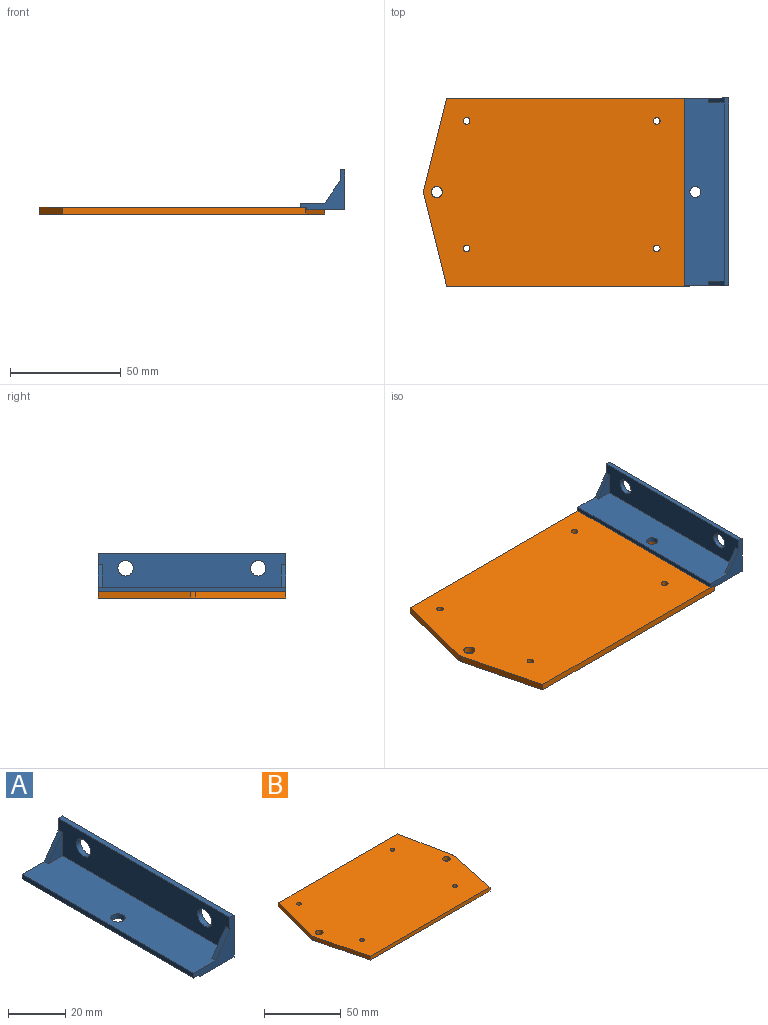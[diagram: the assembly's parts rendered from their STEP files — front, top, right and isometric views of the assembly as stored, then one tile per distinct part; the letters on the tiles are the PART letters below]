
ASSEMBLY  parts=2 mates=1
PART A: 19 faces, bbox 20x85x18 mm
  f0: plane 85x15mm, normal (-1,0,0), area 1158mm2, adj f1,f2,f3,f12,f13,f14,f15,f16
  f1: plane 85x18mm, normal (0,0,1), area 1482.4mm2, adj f0,f2,f3,f4,f5,f15,f16,f17
  f2: plane 20x18mm, normal (0,-1,0), area 122mm2, adj f0,f1,f4,f6,f7,f10,f11,f12
  f3: plane 20x18mm, normal (0,1,0), area 122mm2, adj f0,f1,f4,f6,f8,f10,f11,f12
  f4: plane 85x2mm, normal (-1,0,0), area 170mm2, adj f1,f2,f3,f6
  f5: cylinder r=2.5mm len=5mm, axis (0,0,1), area 31.4mm2, adj f1,f6
  f6: plane 85x11.5mm, normal (0,0,-1), area 602.1mm2, adj f2,f3,f4,f5,f7,f8,f9
  f7: plane 41.21x8.37mm, normal (-0.98,0.2,0), area 42mm2, adj f2,f6,f9,f11
  f8: plane 41.21x8.37mm, normal (-0.98,-0.2,0), area 42mm2, adj f3,f6,f9,f11
  f9: cylinder r=6.5mm len=2.59mm, axis (0,0,1), area 2.6mm2, adj f6,f7,f8,f11
  f10: plane 85x18mm, normal (1,0,0), area 1453mm2, adj f2,f3,f11,f12,f13,f14
  f11: plane 85x17mm, normal (0,0,-1), area 1078.2mm2, adj f2,f3,f7,f8,f9,f10
  f12: plane 85x2mm, normal (0,0,1), area 170mm2, adj f0,f2,f3,f10
  f13: cylinder r=3.5mm len=7mm, axis (1,0,0), area 44mm2, adj f0,f10
  f14: cylinder r=3.5mm len=7mm, axis (1,0,0), area 44mm2, adj f0,f10
  f15: plane 10x7mm, normal (-0.82,0,0.57), area 24.4mm2, adj f0,f1,f3,f16
  f16: plane 10x7mm, normal (0,-1,0), area 35mm2, adj f0,f1,f15
  f17: plane 10x7mm, normal (-0.82,0,0.57), area 24.4mm2, adj f0,f1,f2,f18
  f18: plane 10x7mm, normal (0,1,0), area 35mm2, adj f0,f1,f17
PART B: 16 faces, bbox 129x85x3 mm
  f0: plane 41.25x8.38mm, normal (0.98,0.2,0), area 126.3mm2, adj f1,f12,f14,f15
  f1: plane 110x3mm, normal (0,1,0), area 330mm2, adj f0,f2,f14,f15
  f2: plane 41.7x10.46mm, normal (-0.97,0.24,0), area 129mm2, adj f1,f3,f14,f15
  f3: cylinder r=4.04mm len=3mm, axis (0,0,-1), area 7mm2, adj f2,f4,f14,f15
  f4: plane 41.02x10.26mm, normal (-0.97,-0.24,0), area 126.9mm2, adj f3,f5,f14,f15
  f5: plane 110x3mm, normal (0,-1,0), area 330mm2, adj f4,f6,f14,f15
  f6: plane 41.36x8.38mm, normal (0.98,-0.2,0), area 126.6mm2, adj f5,f12,f14,f15
  f7: cylinder r=1.5mm len=3mm, axis (0,0,-1), area 28.3mm2, adj f14,f15
  f8: cylinder r=1.5mm len=3mm, axis (0,0,-1), area 28.3mm2, adj f14,f15
  f9: cylinder r=1.5mm len=3mm, axis (0,0,-1), area 28.3mm2, adj f14,f15
  f10: cylinder r=2.5mm len=5mm, axis (0,0,-1), area 47.1mm2, adj f14,f15
  f11: cylinder r=2.5mm len=5mm, axis (0,0,-1), area 47.1mm2, adj f14,f15
  f12: cylinder r=6mm len=3mm, axis (0,0,-1), area 7.2mm2, adj f0,f6,f14,f15
  f13: cylinder r=1.5mm len=3mm, axis (0,0,-1), area 28.3mm2, adj f14,f15
  f14: plane 129.04x85mm, normal (0,0,1), area 10101.1mm2, adj f0,f1,f2,f3,f4,f5,f6,f7
  f15: plane 129.04x85mm, normal (0,0,-1), area 10101.1mm2, adj f0,f1,f2,f3,f4,f5,f6,f7
PLACE A t=(-30.12,-24.01,-11.6)mm
PLACE B t=(-102.62,-24.06,-16.6)mm
MATE fastened B.f10 <-> A.f5  axis (0,0,1) through (-45.12,-24.01,-13.6)mm
